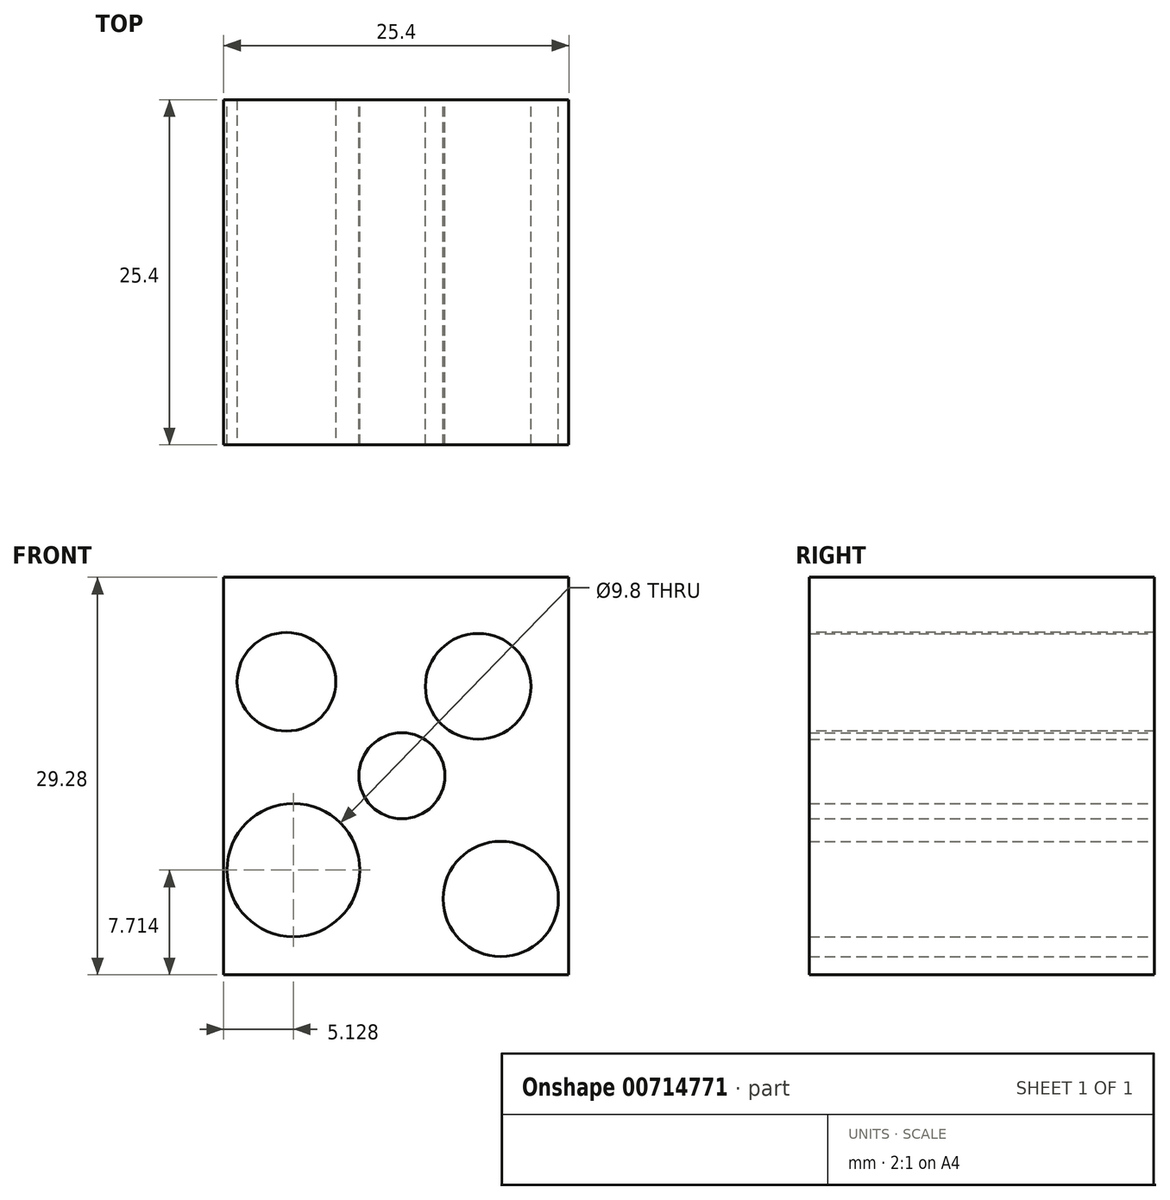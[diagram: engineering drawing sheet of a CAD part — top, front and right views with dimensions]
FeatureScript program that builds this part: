
annotation { "Feature Type Name" : "Feature", "Feature Type Description" : "" }
export const myFeature = defineFeature(function(context is Context, id is Id, definition is map)
    precondition{}
    {
        {
            var Q0;
            Q0=qCreatedBy(makeId("Front.planeOp"),FACE);
            var sketch = newSketch(context, id + "F0", { "sketchPlane" : qUnion([Q0])});
            skLineSegment(sketch, "E0.bottom", {"start": v(-13.11, 13.64) * mm, "end": v(12.29, 13.64) * mm});
            skLineSegment(sketch, "E0.top", {"start": v(-13.11, -15.64) * mm, "end": v(12.29, -15.64) * mm});
            skLineSegment(sketch, "E0.left", {"start": v(-13.11, 13.64) * mm, "end": v(-13.11, -15.64) * mm});
            skLineSegment(sketch, "E0.right", {"start": v(12.29, 13.64) * mm, "end": v(12.29, -15.64) * mm});
            skSolve(sketch);
        }
        {
            var Q0;
            Q0=makeQuery(id+"F0.imprint","IMPRINT",FACE,{"disambiguationData":[TD([[makeQuery(id+"F0.imprint","IMPRINT",EDGE,{"derivedFrom":sQuery(id+"F0.wireOp",EDGE,"E0.bottom")}),-1.0]])]});
            extrude(context, id + "F1", {"entities" : qUnion([Q0]), "depth" : 25.4 * mm, "offsetDistance" : 25.4 * mm});
        }
        {
            var Q0;
            Q0=makeQuery(id+"F1.opExtrude","CAP_FACE",FACE,{"disambiguationData":[OSD([sQuery(id+"F0.wireOp",EDGE,"E0.bottom"),sQuery(id+"F0.wireOp",EDGE,"E0.top"),sQuery(id+"F0.wireOp",EDGE,"E0.left"),sQuery(id+"F0.wireOp",EDGE,"E0.right")])],"isStart":false});
            var sketch = newSketch(context, id + "F2", { "sketchPlane" : qUnion([Q0])});
            skCircle(sketch, "E1", {"center": v(-8.5, 5.94) * mm, "radius": 3.63 * mm});
            skSolve(sketch);
        }
        {
            var Q0;
            Q0=makeQuery(id+"F2.imprint","IMPRINT",FACE,{"disambiguationData":[TD([[makeQuery(id+"F2.imprint","IMPRINT",EDGE,{"derivedFrom":sQuery(id+"F2.wireOp",EDGE,"E1")}),1.0]])]});
            extrude(context, id + "F3", {"entities" : qUnion([Q0]), "operationType" : NewBodyOperationType.REMOVE, "oppositeDirection" : true, "depth" : 30.23 * mm, "offsetDistance" : 25.4 * mm});
        }
        {
            var Q0;
            Q0=makeQuery(id+"F1.opExtrude","CAP_FACE",FACE,{"disambiguationData":[OSD([sQuery(id+"F0.wireOp",EDGE,"E0.bottom"),sQuery(id+"F0.wireOp",EDGE,"E0.top"),sQuery(id+"F0.wireOp",EDGE,"E0.left"),sQuery(id+"F0.wireOp",EDGE,"E0.right")])],"isStart":true});
            var sketch = newSketch(context, id + "F4", { "sketchPlane" : qUnion([Q0])});
            skCircle(sketch, "E2", {"center": v(0, -0.98) * mm, "radius": 3.16 * mm});
            skCircle(sketch, "E3", {"center": v(-5.62, 5.6) * mm, "radius": 3.89 * mm});
            skCircle(sketch, "E4", {"center": v(-7.28, -10.05) * mm, "radius": 4.24 * mm});
            skCircle(sketch, "E5", {"center": v(7.98, -7.93) * mm, "radius": 4.9 * mm});
            skSolve(sketch);
        }
        {
            var Q0;
            Q0=makeQuery(id+"F4.imprint","IMPRINT",FACE,{"disambiguationData":[TD([[makeQuery(id+"F4.imprint","IMPRINT",EDGE,{"derivedFrom":sQuery(id+"F4.wireOp",EDGE,"E2")}),1.0]])]});
            var Q1;
            Q1=makeQuery(id+"F4.imprint","IMPRINT",FACE,{"disambiguationData":[TD([[makeQuery(id+"F4.imprint","IMPRINT",EDGE,{"derivedFrom":sQuery(id+"F4.wireOp",EDGE,"E5")}),1.0]])]});
            var Q2;
            Q2=makeQuery(id+"F4.imprint","IMPRINT",FACE,{"disambiguationData":[TD([[makeQuery(id+"F4.imprint","IMPRINT",EDGE,{"derivedFrom":sQuery(id+"F4.wireOp",EDGE,"E4")}),1.0]])]});
            var Q3;
            Q3=makeQuery(id+"F4.imprint","IMPRINT",FACE,{"disambiguationData":[TD([[makeQuery(id+"F4.imprint","IMPRINT",EDGE,{"derivedFrom":sQuery(id+"F4.wireOp",EDGE,"E3")}),1.0]])]});
            extrude(context, id + "F5", {"entities" : qUnion([Q0, Q1, Q2, Q3]), "operationType" : NewBodyOperationType.REMOVE, "endBound" : BoundingType.THROUGH_ALL, "oppositeDirection" : true, "depth" : 25.4 * mm, "offsetDistance" : 25.4 * mm});
        }
    });
